# Revit family: IS_ConnectAir_Multiproduct_BIM_DE;E0365;E0366
name_source: partatom
category: Plumbing Fixtures
revit_build: Autodesk Revit MEP 2014 (Build: 20130308_1515(x64)
units: mm (PartAtom-declared; Revit-internal decimal feet)

## types (2) — shared parameters
Accessories = www.idealstandard.de\ersatzteile
AreaUnits = millimeters
Assembly Code = C1030200
AssetType = Fixed
Brand = Ideal Standard
ConnectionType = Mechanical
DurationUnit = year
ExpectedLife = 25
Finish = white
GrossWeight = 0
IfcExportAs = IfcSanitaryTerminalType
IfcExportType = SEAT&COVER
InstallationInstructions = www.idealstandard.de\produkte
LinearUnits = millimeters
ManufacturerURL = www.idealstandard.com
NBSDescription = WC Seats and covers
NettWeight = 2,2 kg
NominalHeight = 50 mm  [stored 0.164042 ft]
NominalLength = 445 mm  [stored 1.45997 ft]
NominalWidth = 365 mm  [stored 1.19751 ft]
PanColor = White
PanMaterial = Duroplast
ProductInformation = www.idealstandard.de/produkte
Shape = Sculptured
Size = 365x445x50mm
Space = Internal
URL = www.idealstandard.com
Uniclass2015Code = Pr_40_20_93_95
Uniclass2015Title = WC Seats and covers
Uniclass2015Version = Products v1.1
Version = 1
VolumeUnits = Litres
WarrantyDescription = Manufacturers Warranty
WarrantyDurationUnit = year
zero-valued in all types: CWFU, Cost, Default Elevation, HWFU, SpilloverLevel, WFU

## per-type parameters (varying)
| type | BIMObjectName | BarCode | Description | Features | Model | ModelNumber | ModelReference | NBSReference | Name |
| E036501  - Connect Air sandwich style seat & cover, slow close | ISI_IdealStandard_WcSeatsAndCovers_ConnectAir_E036501 | 5017830514589 | E036501 Connect Air sandwich style seat & cover, slow close | Connect Air sandwich style seat & cover, slow close | E036501 | E036501 | Connect Air sandwich style seat & cover, slow close | 45-30-70/387 | WcSeatsAndCovers_ConnectAir_E036501_IdealStandard |
| E036601 - Connect Air sandwich style seat & cover | ISI_IdealStandard_WcSeatsAndCovers_ConnectAir_E036601 | 5017830514596 | E036601 Connect Air sandwich style seat & cover | Connect Air sandwich style seat & cover | E036601 | E036601 | Connect Air sandwich style seat & cover | 45-30-70/384 | WcSeatsAndCovers_ConnectAir_E036601_IdealStandard |

note: [stored X ft] marks values corroborated as IEEE doubles in the binary element streams (Revit-internal decimal feet)

## geometry (parser evidence)
native form markers: Sweep x2
no freeform markers — native parametric forms only
